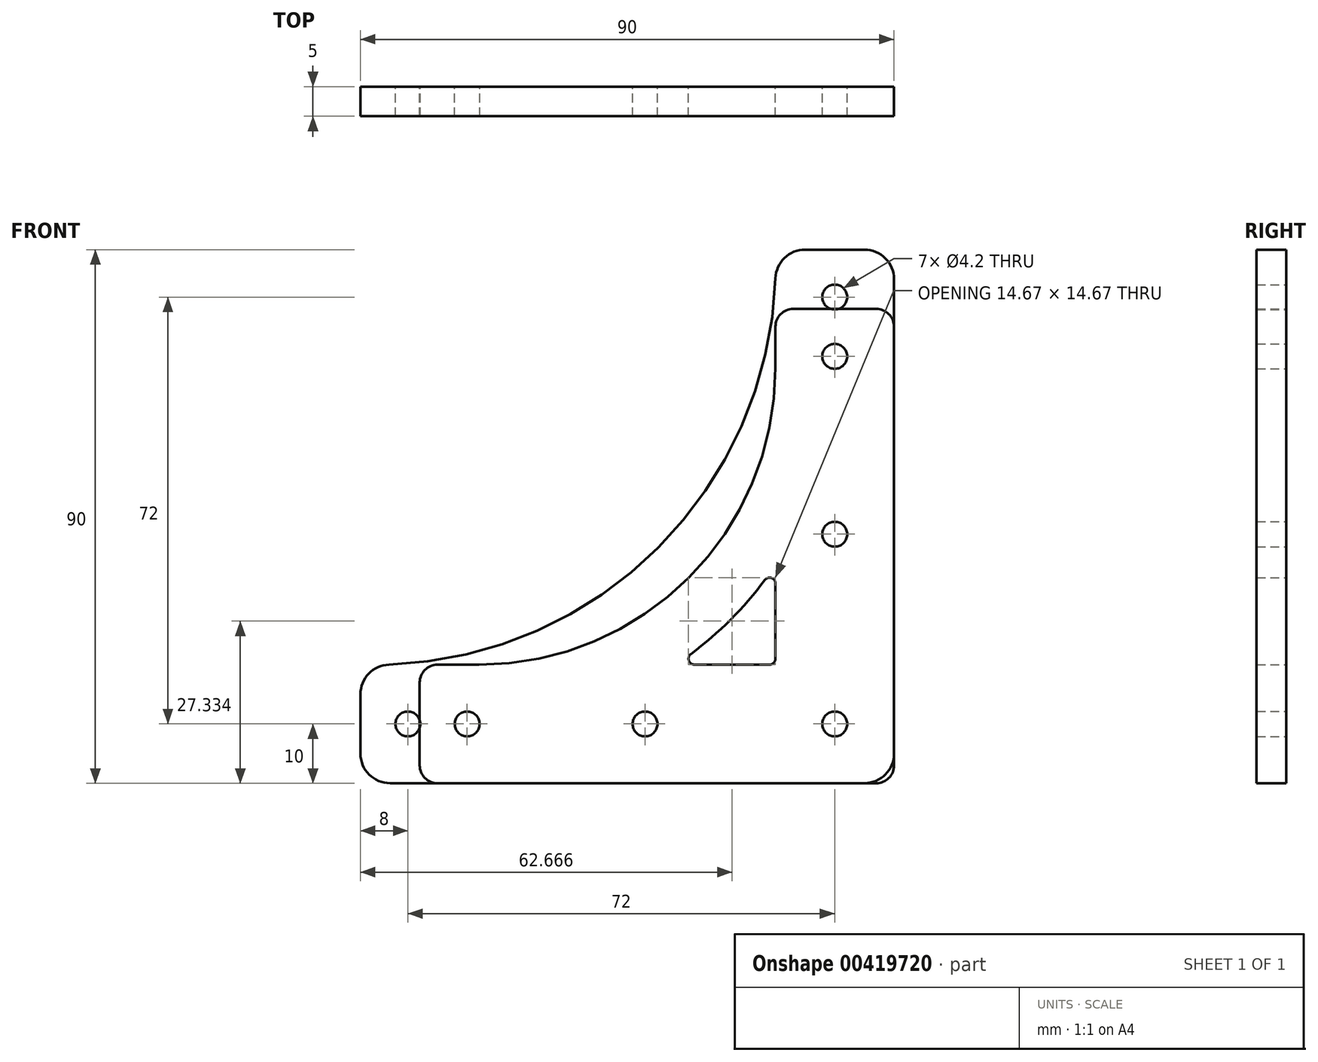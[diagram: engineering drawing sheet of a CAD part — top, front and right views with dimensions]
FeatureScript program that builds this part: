
annotation { "Feature Type Name" : "Feature", "Feature Type Description" : "" }
export const myFeature = defineFeature(function(context is Context, id is Id, definition is map)
    precondition{}
    {
        {
            var Q0;
            Q0=qCreatedBy(makeId("Front.planeOp"),FACE);
            var sketch = newSketch(context, id + "F0", { "sketchPlane" : qUnion([Q0])});
            skLineSegment(sketch, "E0", {"start": v(0, 0) * mm, "end": v(0, 80) * mm, "construction": true});
            skLineSegment(sketch, "E1", {"start": v(0, 80) * mm, "end": v(-80, 0) * mm, "construction": true});
            skLineSegment(sketch, "E2", {"start": v(-80, 5) * mm, "end": v(-80, 0) * mm});
            skLineSegment(sketch, "E3", {"start": v(-5, 80) * mm, "end": v(0, 80) * mm});
            skLineSegment(sketch, "E4", {"start": v(0, 0) * mm, "end": v(-80, 0) * mm, "construction": true});
            skArc(sketch, "E5", {"start": v(-75.18, 10) * mm, "mid": v(-29.77, 29.77) * mm, "end": v(-10, 75.18) * mm});
            skCircle(sketch, "E6", {"center": v(0, 72) * mm, "radius": 2.1 * mm});
            skCircle(sketch, "E7", {"center": v(-72, 0) * mm, "radius": 2.1 * mm});
            skLineSegment(sketch, "E8.MirrorCS", {"start": v(5, 80) * mm, "end": v(0, 80) * mm});
            skLineSegment(sketch, "E9.MirrorCS", {"start": v(-80, -5) * mm, "end": v(-80, 0) * mm});
            skPoint(sketch, "E10.visualSharp", {"position": v(-80, 10) * mm});
            skArc(sketch, "E10.filletArc", {"start": v(-75.18, 10) * mm, "mid": v(-78.6, 8.48) * mm, "end": v(-80, 5) * mm});
            skPoint(sketch, "E11.visualSharp", {"position": v(-10, 80) * mm});
            skArc(sketch, "E11.filletArc", {"start": v(-5, 80) * mm, "mid": v(-8.48, 78.6) * mm, "end": v(-10, 75.18) * mm});
            skPoint(sketch, "E12.visualSharp", {"position": v(10, 80) * mm});
            skArc(sketch, "E12.filletArc", {"start": v(10, 75) * mm, "mid": v(8.54, 78.54) * mm, "end": v(5, 80) * mm});
            skPoint(sketch, "E13.visualSharp", {"position": v(-80, -10) * mm});
            skArc(sketch, "E13.filletArc", {"start": v(-80, -5) * mm, "mid": v(-78.54, -8.54) * mm, "end": v(-75, -10) * mm});
            skLineSegment(sketch, "E14", {"start": v(-75, -10) * mm, "end": v(5, -10) * mm});
            skLineSegment(sketch, "E15", {"start": v(10, 75) * mm, "end": v(10, -5) * mm});
            skArc(sketch, "E16.filletArc", {"start": v(5, -10) * mm, "mid": v(8.54, -8.54) * mm, "end": v(10, -5) * mm});
            skCircle(sketch, "E17", {"center": v(-32, 0) * mm, "radius": 2.1 * mm});
            skCircle(sketch, "E18", {"center": v(0, 32) * mm, "radius": 2.1 * mm});
            skCircle(sketch, "E19", {"center": v(0, 0) * mm, "radius": 2.1 * mm});
            skSolve(sketch);
        }
        {
            var Q0;
            Q0 = qSketchRegion(id + "F0", true);
            extrude(context, id + "F1", {"entities" : qUnion([Q0]), "depth" : 5 * mm, "offsetDistance" : 25 * mm});
        }
        {
            var Q0;
            Q0=qCreatedBy(makeId("Front.planeOp"),FACE);
            var sketch = newSketch(context, id + "F2", { "sketchPlane" : qUnion([Q0])});
            skLineSegment(sketch, "E20", {"start": v(0, 0) * mm, "end": v(0, 70) * mm, "construction": true});
            skLineSegment(sketch, "E21", {"start": v(0, 0) * mm, "end": v(-70, 0) * mm, "construction": true});
            skLineSegment(sketch, "E22", {"start": v(0, 70) * mm, "end": v(-7, 70) * mm});
            skLineSegment(sketch, "E23", {"start": v(-10, 67) * mm, "end": v(-10, 60) * mm});
            skLineSegment(sketch, "E24", {"start": v(0, 70) * mm, "end": v(7, 70) * mm});
            skLineSegment(sketch, "E25", {"start": v(10, 67) * mm, "end": v(10, -7) * mm});
            skLineSegment(sketch, "E26", {"start": v(7, -10) * mm, "end": v(-67, -10) * mm});
            skLineSegment(sketch, "E27", {"start": v(-70, -7) * mm, "end": v(-70, 0) * mm});
            skLineSegment(sketch, "E28", {"start": v(-70, 0) * mm, "end": v(-70, 7) * mm});
            skLineSegment(sketch, "E29", {"start": v(-67, 10) * mm, "end": v(-60, 10) * mm});
            skArc(sketch, "E30", {"start": v(-60, 10) * mm, "mid": v(-24.64, 24.64) * mm, "end": v(-10, 60) * mm});
            skCircle(sketch, "E31", {"center": v(-62, 0) * mm, "radius": 2.1 * mm});
            skCircle(sketch, "E32", {"center": v(0, 62) * mm, "radius": 2.1 * mm});
            skArc(sketch, "E33.0", {"start": v(-24.26, 11.8) * mm, "mid": v(-17.57, 17.57) * mm, "end": v(-11.8, 24.26) * mm});
            skPoint(sketch, "E34.visualSharp", {"position": v(0, 60) * mm});
            skPoint(sketch, "E35.visualSharp", {"position": v(-60, 0) * mm});
            skPoint(sketch, "E36.visualSharp", {"position": v(0, 0) * mm});
            skLineSegment(sketch, "E37", {"start": v(-60, 10) * mm, "end": v(0, 10) * mm, "construction": true});
            skLineSegment(sketch, "E38", {"start": v(-10, 60) * mm, "end": v(-10, 10) * mm, "construction": true});
            skLineSegment(sketch, "E39", {"start": v(-23.67, 10) * mm, "end": v(-11, 10) * mm});
            skLineSegment(sketch, "E40", {"start": v(-10, 23.67) * mm, "end": v(-10, 11) * mm});
            skPoint(sketch, "E41.visualSharp", {"position": v(-10, 26.83) * mm});
            skArc(sketch, "E41.filletArc", {"start": v(-10, 23.67) * mm, "mid": v(-10.69, 24.62) * mm, "end": v(-11.8, 24.26) * mm});
            skPoint(sketch, "E42.visualSharp", {"position": v(-26.83, 10) * mm});
            skArc(sketch, "E42.filletArc", {"start": v(-24.26, 11.8) * mm, "mid": v(-24.62, 10.69) * mm, "end": v(-23.67, 10) * mm});
            skPoint(sketch, "E43.visualSharp", {"position": v(-10, 10) * mm});
            skArc(sketch, "E43.filletArc", {"start": v(-11, 10) * mm, "mid": v(-10.3, 10.3) * mm, "end": v(-10, 11) * mm});
            skPoint(sketch, "E44.visualSharp", {"position": v(-70, 10) * mm});
            skArc(sketch, "E44.filletArc", {"start": v(-67, 10) * mm, "mid": v(-69.12, 9.12) * mm, "end": v(-70, 7) * mm});
            skPoint(sketch, "E45.visualSharp", {"position": v(-70, -10) * mm});
            skArc(sketch, "E45.filletArc", {"start": v(-70, -7) * mm, "mid": v(-69.12, -9.12) * mm, "end": v(-67, -10) * mm});
            skPoint(sketch, "E46.visualSharp", {"position": v(10, -10) * mm});
            skArc(sketch, "E46.filletArc", {"start": v(7, -10) * mm, "mid": v(9.12, -9.12) * mm, "end": v(10, -7) * mm});
            skPoint(sketch, "E47.visualSharp", {"position": v(10, 70) * mm});
            skArc(sketch, "E47.filletArc", {"start": v(10, 67) * mm, "mid": v(9.12, 69.12) * mm, "end": v(7, 70) * mm});
            skPoint(sketch, "E48.visualSharp", {"position": v(-10, 70) * mm});
            skArc(sketch, "E48.filletArc", {"start": v(-7, 70) * mm, "mid": v(-9.12, 69.12) * mm, "end": v(-10, 67) * mm});
            skSolve(sketch);
        }
        {
            var Q0;
            Q0 = qSketchRegion(id + "F2", true);
            extrude(context, id + "F3", {"entities" : qUnion([Q0]), "depth" : 5 * mm, "offsetDistance" : 25 * mm});
        }
    });
